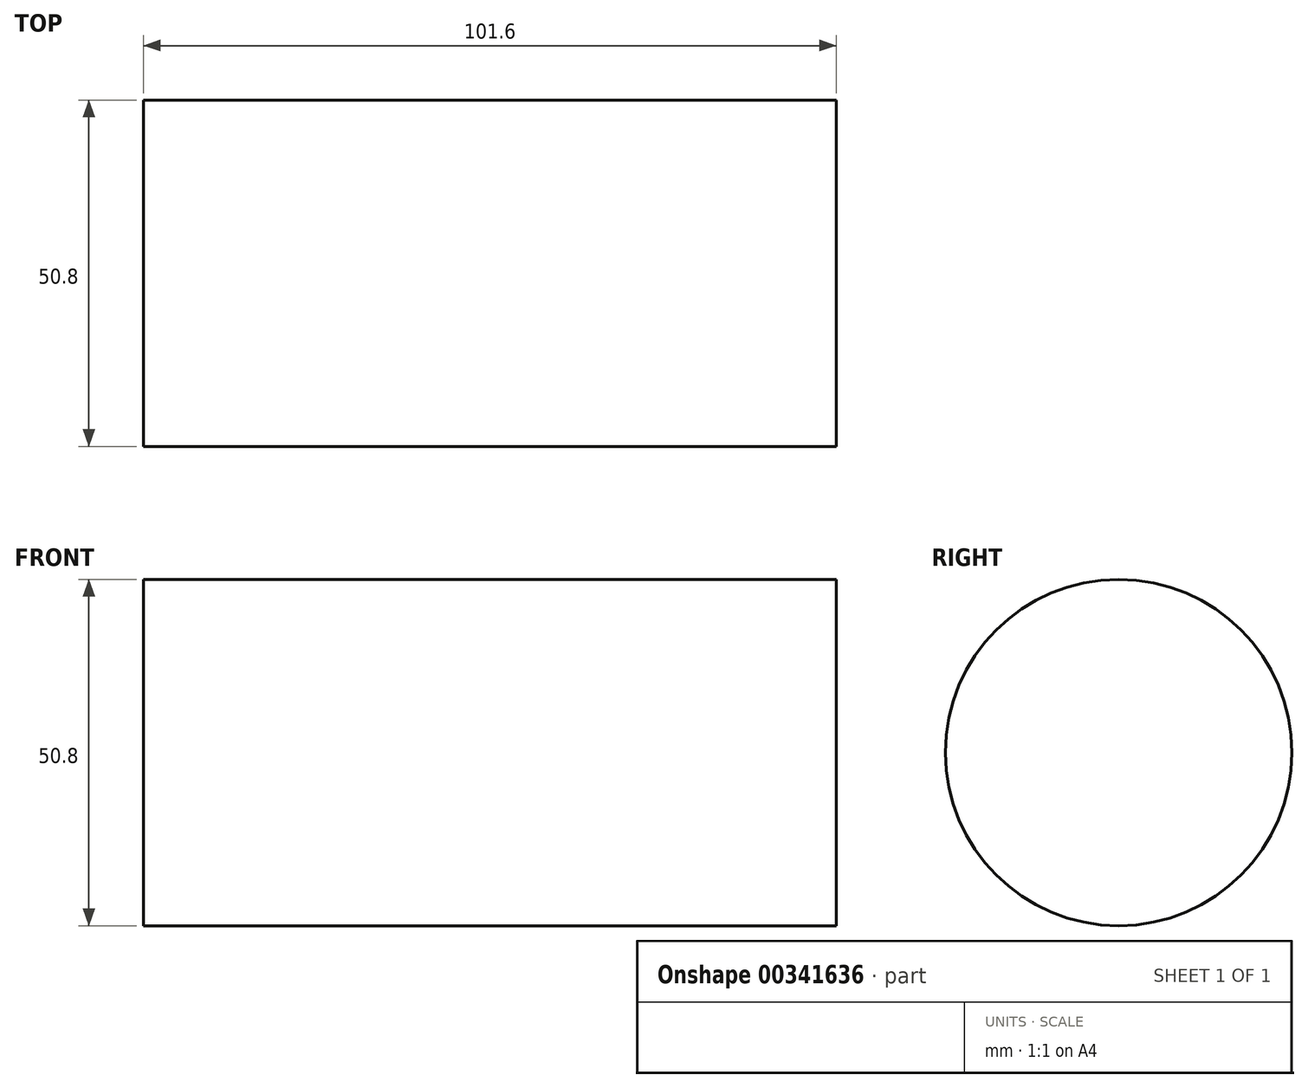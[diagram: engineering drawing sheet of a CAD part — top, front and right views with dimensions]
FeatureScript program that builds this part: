
annotation { "Feature Type Name" : "Feature", "Feature Type Description" : "" }
export const myFeature = defineFeature(function(context is Context, id is Id, definition is map)
    precondition{}
    {
        {
            var Q0;
            Q0=qCreatedBy(makeId("Right.planeOp"),FACE);
            var sketch = newSketch(context, id + "F0", { "sketchPlane" : qUnion([Q0])});
            skCircle(sketch, "E0", {"center": v(0, 0) * mm, "radius": 25.4 * mm});
            skSolve(sketch);
        }
        {
            var Q0;
            Q0 = qSketchRegion(id + "F0", true);
            extrude(context, id + "F1", {"entities" : qUnion([Q0]), "depth" : 101.6 * mm});
        }
    });
